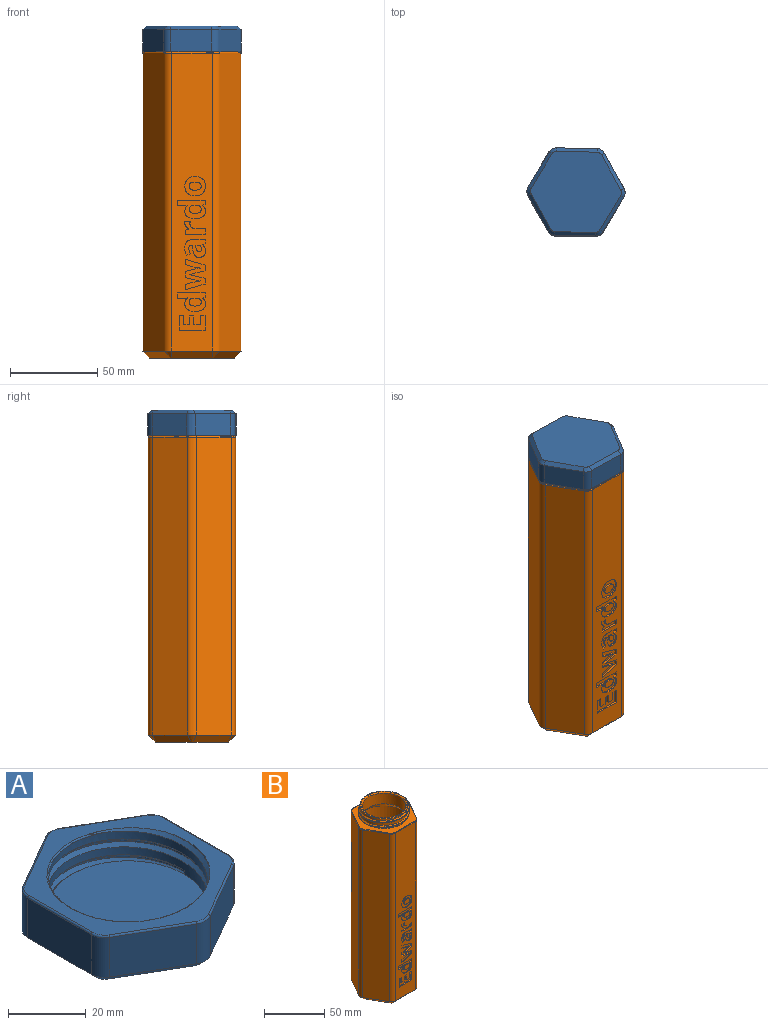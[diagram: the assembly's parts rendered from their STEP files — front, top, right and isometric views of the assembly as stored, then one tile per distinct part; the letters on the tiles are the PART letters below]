
ASSEMBLY  parts=2 mates=1
PART A: 48 faces, bbox 50.8x57x16.4 mm
  f0: cylinder r=20.5mm len=41mm, axis (0,0,1), area 638.7mm2, adj f9,f10,f12,f13,f15,f47
  f1: plane 20x12.5mm, normal (0.5,-0.87,0), area 288.7mm2, adj f16,f21,f26,f34
  f2: plane 23.09x12.5mm, normal (1,0,0), area 288.7mm2, adj f16,f17,f22,f37
  f3: plane 20x12.5mm, normal (0.5,0.87,0), area 288.7mm2, adj f17,f18,f25,f41
  f4: plane 20x12.5mm, normal (-0.5,0.87,0), area 288.7mm2, adj f18,f19,f29,f45
  f5: plane 23.09x12.5mm, normal (-1,0,0), area 288.7mm2, adj f19,f20,f33,f42
  f6: plane 20x12.5mm, normal (-0.5,-0.87,0), area 288.7mm2, adj f20,f21,f30,f38
  f7: plane 55.19x49mm, normal (0,0,1), area 683.1mm2, adj f10,f13,f14,f15,f22,f23,f24,f25
  f8: plane 52.19x46mm, normal (0,0,-1), area 1829.6mm2, adj f34,f35,f36,f37,f38,f39,f40,f41
  f9: plane 41x41mm, normal (0,0,1), area 1320.3mm2, adj f0,f11
  f10: torus R=20.9mm, axis (0,0,1), area 45.3mm2, adj f0,f7,f13,f15
  f11: cylinder r=20.5mm len=20.5mm, axis (0,0,-1), area 20.1mm2, adj f9,f12,f13
  f12: plane 2.36x0.9mm, normal (0,1,0), area 1.3mm2, adj f0,f11,f13,f46,f47
  f13: bspline ~49.65x43mm, area 400.1mm2, adj f0,f7,f10,f11,f12,f14,f46
  f14: cylinder r=21.5mm len=43mm, axis (0,0,-1), area 135.1mm2, adj f7,f13,f15,f46
  f15: bspline ~49.65x43mm, area 343.9mm2, adj f0,f7,f10,f14,f46,f47
  f16: cylinder r=5mm len=12.5mm, axis (0,0,-1), area 65.4mm2, adj f1,f2,f24,f35
  f17: cylinder r=5mm len=12.5mm, axis (0,0,-1), area 65.4mm2, adj f2,f3,f23,f39
  f18: cylinder r=5mm len=12.5mm, axis (0,0,-1), area 65.4mm2, adj f3,f4,f27,f43
  f19: cylinder r=5mm len=12.5mm, axis (0,0,-1), area 65.4mm2, adj f4,f5,f31,f44
  f20: cylinder r=5mm len=12.5mm, axis (0,0,-1), area 65.4mm2, adj f5,f6,f32,f40
  f21: cylinder r=5mm len=12.5mm, axis (0,0,-1), area 65.4mm2, adj f1,f6,f28,f36
  f22: cylinder r=0.5mm len=23.09mm, axis (0,-1,0), area 18.1mm2, adj f2,f7,f23,f24
  f23: torus R=4.5mm, axis (0,0,1), area 4mm2, adj f7,f17,f22,f25
  f24: torus R=4.5mm, axis (0,0,1), area 4mm2, adj f7,f16,f22,f26
  f25: cylinder r=0.5mm len=20.25mm, axis (0.87,-0.5,0), area 18.1mm2, adj f3,f7,f23,f27
  f26: cylinder r=0.5mm len=20.25mm, axis (-0.87,-0.5,0), area 18.1mm2, adj f1,f7,f24,f28
  f27: torus R=4.5mm, axis (0,0,1), area 4mm2, adj f7,f18,f25,f29
  f28: torus R=4.5mm, axis (0,0,1), area 4mm2, adj f7,f21,f26,f30
  f29: cylinder r=0.5mm len=20.25mm, axis (0.87,0.5,0), area 18.1mm2, adj f4,f7,f27,f31
  f30: cylinder r=0.5mm len=20.25mm, axis (-0.87,0.5,0), area 18.1mm2, adj f6,f7,f28,f32
  f31: torus R=4.5mm, axis (0,0,1), area 4mm2, adj f7,f19,f29,f33
  f32: torus R=4.5mm, axis (0,0,1), area 4mm2, adj f7,f20,f30,f33
  f33: cylinder r=0.5mm len=23.09mm, axis (0,1,0), area 18.1mm2, adj f5,f7,f31,f32
  f34: plane 21x13.28mm, normal (0.35,-0.61,-0.71), area 65.3mm2, adj f1,f8,f35,f36
  f35: cone r=3mm half-angle=45deg, axis (0,0,1), area 11.8mm2, adj f8,f16,f34,f37
  f36: cone r=3mm half-angle=45deg, axis (0,0,1), area 11.8mm2, adj f8,f21,f34,f38
  f37: plane 23.09x2mm, normal (0.71,0,-0.71), area 65.3mm2, adj f2,f8,f35,f39
  f38: plane 21x13.28mm, normal (-0.35,-0.61,-0.71), area 65.3mm2, adj f6,f8,f36,f40
  f39: cone r=3mm half-angle=45deg, axis (0,0,1), area 11.8mm2, adj f8,f17,f37,f41
  f40: cone r=3mm half-angle=45deg, axis (0,0,1), area 11.8mm2, adj f8,f20,f38,f42
  f41: plane 21x13.28mm, normal (0.35,0.61,-0.71), area 65.3mm2, adj f3,f8,f39,f43
  f42: plane 23.09x2mm, normal (-0.71,0,-0.71), area 65.3mm2, adj f5,f8,f40,f44
  f43: cone r=3mm half-angle=45deg, axis (0,0,1), area 11.8mm2, adj f8,f18,f41,f45
  f44: cone r=3mm half-angle=45deg, axis (0,0,1), area 11.8mm2, adj f8,f19,f42,f45
  f45: plane 21x13.28mm, normal (-0.35,0.61,-0.71), area 65.3mm2, adj f4,f8,f43,f44
  f46: cylinder r=0.1mm len=0.6mm, axis (0,0,-1), area 0.1mm2, adj f12,f13,f14,f15,f47
  f47: bspline ~1.47x1.47mm, area 0.2mm2, adj f0,f12,f15,f46
PART B: 211 faces, bbox 57.4x51.2x186.9 mm
  f0: plane 170.5x23.09mm, normal (0,-1,0), area 3247.6mm2, adj f17,f18,f36,f53,f60,f61,f62,f63
  f1: cylinder r=20mm len=40mm, axis (0,0,-1), area 682.5mm2, adj f2,f3,f9,f11,f14,f16
  f2: plane 2.3x1mm, normal (0,1,0), area 1.5mm2, adj f1,f3,f11,f12,f13,f16,f27,f28
  f3: bspline ~48.5x42mm, area 319.4mm2, adj f1,f2,f9,f16,f27
  f4: plane 170.5x20mm, normal (-0.87,-0.5,0), area 3937.5mm2, adj f17,f22,f40,f49
  f5: plane 170.5x20mm, normal (0.87,-0.5,0), area 3937.5mm2, adj f18,f19,f32,f57
  f6: plane 170.5x20mm, normal (0.87,0.5,0), area 3937.5mm2, adj f19,f20,f35,f54
  f7: plane 170.5x23.09mm, normal (0,1,0), area 3937.5mm2, adj f20,f21,f39,f50
  f8: plane 170.5x20mm, normal (-0.87,0.5,0), area 3937.5mm2, adj f21,f22,f43,f46
  f9: plane 55.57x49.38mm, normal (0,0,1), area 777.8mm2, adj f1,f3,f11,f12,f27,f28,f32,f33
  f10: plane 48.19x42mm, normal (0,0,-1), area 1492.5mm2, adj f44,f46,f47,f48,f49,f50,f51,f52
  f11: bspline ~48.5x42mm, area 268.8mm2, adj f1,f2,f9,f28
  f12: cylinder r=21mm len=42mm, axis (0,0,-1), area 66.2mm2, adj f2,f9,f27,f28
  f13: plane 0.93x0.06mm, normal (0,0,1), area 0mm2, adj f2,f14,f16
  f14: torus R=19.8mm, axis (0,0,1), area 39.3mm2, adj f1,f13,f15
  f15: plane 39.6x39.6mm, normal (0,0,1), area 97.5mm2, adj f14,f59
  f16: bspline ~10.06x3.04mm, area 1.4mm2, adj f1,f2,f3,f13
  f17: cylinder r=5mm len=170.5mm, axis (0,0,-1), area 892.7mm2, adj f0,f4,f38,f51
  f18: cylinder r=5mm len=170.5mm, axis (0,0,-1), area 892.7mm2, adj f0,f5,f34,f55
  f19: cylinder r=5mm len=170.5mm, axis (0,0,-1), area 892.7mm2, adj f5,f6,f33,f56
  f20: cylinder r=5mm len=170.5mm, axis (0,0,-1), area 892.7mm2, adj f6,f7,f37,f52
  f21: cylinder r=5mm len=170.5mm, axis (0,0,-1), area 892.7mm2, adj f7,f8,f41,f48
  f22: cylinder r=5mm len=170.5mm, axis (0,0,-1), area 892.7mm2, adj f4,f8,f42,f47
  f23: plane 36x36mm, normal (0,0,1), area 1004.7mm2, adj f31,f58
  f24: cylinder r=22mm len=159.46mm, axis (0,0,-1), area 22042.6mm2, adj f25,f58
  f25: cone r=22mm half-angle=40deg, axis (0,0,-1), area 782mm2, adj f24,f26
  f26: cylinder r=18mm len=36mm, axis (0,0,-1), area 1218mm2, adj f25,f59
  f27: bspline ~42.02x42.01mm, area 46.5mm2, adj f2,f3,f9,f12
  f28: bspline ~42.02x42.01mm, area 44.1mm2, adj f2,f9,f11,f12
  f29: cone r=1.5mm half-angle=26.3deg, axis (0,0.17,-0.98), area 19.6mm2, adj f44,f45
  f30: cylinder r=1.5mm len=3.15mm, axis (0,-0.17,0.98), area 10.7mm2, adj f31,f45
  f31: cone r=3.38mm half-angle=29.1deg, axis (0,0.17,-0.98), area 12mm2, adj f23,f30
  f32: cylinder r=0.5mm len=20.25mm, axis (-0.5,-0.87,0), area 18.1mm2, adj f5,f9,f33,f34
  f33: torus R=4.5mm, axis (0,0,1), area 4mm2, adj f9,f19,f32,f35
  f34: torus R=4.5mm, axis (0,0,1), area 4mm2, adj f9,f18,f32,f36
  f35: cylinder r=0.5mm len=20.25mm, axis (0.5,-0.87,0), area 18.1mm2, adj f6,f9,f33,f37
  f36: cylinder r=0.5mm len=23.09mm, axis (-1,0,0), area 18.1mm2, adj f0,f9,f34,f38
  f37: torus R=4.5mm, axis (0,0,1), area 4mm2, adj f9,f20,f35,f39
  f38: torus R=4.5mm, axis (0,0,1), area 4mm2, adj f9,f17,f36,f40
  f39: cylinder r=0.5mm len=23.09mm, axis (1,0,0), area 18.1mm2, adj f7,f9,f37,f41
  f40: cylinder r=0.5mm len=20.25mm, axis (-0.5,0.87,0), area 18.1mm2, adj f4,f9,f38,f42
  f41: torus R=4.5mm, axis (0,0,1), area 4mm2, adj f9,f21,f39,f43
  f42: torus R=4.5mm, axis (0,0,1), area 4mm2, adj f9,f22,f40,f43
  f43: cylinder r=0.5mm len=20.25mm, axis (0.5,0.87,0), area 18.1mm2, adj f8,f9,f41,f42
  f44: bspline ~6.73x6.6mm, area 10.7mm2, adj f10,f29
  f45: torus R=9.5mm, axis (0,0.17,-0.98), area 41mm2, adj f29,f30
  f46: plane 22x15.01mm, normal (-0.61,0.35,-0.71), area 130.6mm2, adj f8,f10,f47,f48
  f47: cone r=1mm half-angle=45deg, axis (0,0,1), area 17.8mm2, adj f10,f22,f46,f49
  f48: cone r=1mm half-angle=45deg, axis (0,0,1), area 17.8mm2, adj f10,f21,f46,f50
  f49: plane 22x15.01mm, normal (-0.61,-0.35,-0.71), area 130.6mm2, adj f4,f10,f47,f51
  f50: plane 23.09x4mm, normal (0,0.71,-0.71), area 130.6mm2, adj f7,f10,f48,f52
  f51: cone r=1mm half-angle=45deg, axis (0,0,1), area 17.8mm2, adj f10,f17,f49,f53
  f52: cone r=1mm half-angle=45deg, axis (0,0,1), area 17.8mm2, adj f10,f20,f50,f54
  f53: plane 23.09x4mm, normal (0,-0.71,-0.71), area 130.6mm2, adj f0,f10,f51,f55
  f54: plane 22x15.01mm, normal (0.61,0.35,-0.71), area 130.6mm2, adj f6,f10,f52,f56
  f55: cone r=1mm half-angle=45deg, axis (0,0,1), area 17.8mm2, adj f10,f18,f53,f57
  f56: cone r=1mm half-angle=45deg, axis (0,0,1), area 17.8mm2, adj f10,f19,f54,f57
  f57: plane 22x15.01mm, normal (0.61,-0.35,-0.71), area 130.6mm2, adj f5,f10,f55,f56
  f58: cone r=22mm half-angle=45deg, axis (0,0,1), area 710.9mm2, adj f23,f24
  f59: torus R=19mm, axis (0,0,1), area 181.2mm2, adj f15,f26
  f60: extruded ~4.34x1.47mm, area 4.7mm2, adj f0,f61,f77,f78
  f61: extruded ~3.12x1mm, area 3.2mm2, adj f0,f60,f62,f78
  f62: extruded ~2.04x1.92mm, area 2.8mm2, adj f0,f61,f63,f78
  f63: extruded ~2.89x1mm, area 3mm2, adj f0,f62,f64,f78
  f64: extruded ~4.09x1.55mm, area 4.5mm2, adj f0,f63,f65,f78
  f65: extruded ~4.33x1.45mm, area 4.7mm2, adj f0,f64,f66,f78
  f66: extruded ~3.13x1mm, area 3.2mm2, adj f0,f65,f67,f78
  f67: extruded ~2.06x1.92mm, area 2.9mm2, adj f0,f66,f68,f78
  f68: extruded ~2.89x1mm, area 3mm2, adj f0,f67,f77,f78
  f69: extruded ~2.55x1mm, area 2.6mm2, adj f70,f76,f78,f79
  f70: extruded ~2.54x1mm, area 2.6mm2, adj f69,f71,f78,f79
  f71: extruded ~1.79x1mm, area 2.1mm2, adj f70,f72,f78,f79
  f72: extruded ~1.8x1mm, area 2.1mm2, adj f71,f73,f78,f79
  f73: extruded ~2.53x1mm, area 2.6mm2, adj f72,f74,f78,f79
  f74: extruded ~2.56x1mm, area 2.6mm2, adj f73,f75,f78,f79
  f75: extruded ~1.79x1mm, area 2.1mm2, adj f74,f76,f78,f79
  f76: extruded ~1.81x1mm, area 2.1mm2, adj f69,f75,f78,f79
  f77: extruded ~4.08x1.57mm, area 4.5mm2, adj f0,f60,f68,f78
  f78: plane 11.79x11.03mm, normal (0,-1,0), area 79.2mm2, adj f60,f61,f62,f63,f64,f65,f66,f67
  f79: plane 6.8x4.69mm, normal (0,-1,0), area 26.8mm2, adj f69,f70,f71,f72,f73,f74,f75,f76
  f80: extruded ~1.74x1mm, area 1.9mm2, adj f81,f102,f103,f208
  f81: extruded ~1.66x1mm, area 1.9mm2, adj f80,f82,f103,f208
  f82: extruded ~2.52x1mm, area 2.6mm2, adj f81,f83,f103,f208
  f83: extruded ~2.56x1mm, area 2.7mm2, adj f82,f84,f103,f208
  f84: extruded ~1.61x1mm, area 1.9mm2, adj f83,f85,f103,f208
  f85: extruded ~1.84x1mm, area 2.1mm2, adj f84,f86,f103,f208
  f86: extruded ~2.63x1mm, area 2.7mm2, adj f85,f87,f103,f208
  f87: plane 1x0.34mm, normal (0,0,1), area 0.3mm2, adj f86,f102,f103,f208
  f88: extruded ~3.15x1.56mm, area 3.7mm2, adj f0,f89,f101,f103
  f89: extruded ~3.23x1.68mm, area 3.8mm2, adj f0,f88,f90,f103
  f90: plane 1x0.13mm, normal (-1,0,0), area 0.1mm2, adj f0,f89,f91,f103
  f91: plane 1.47x1mm, normal (-0.38,0,0.93), area 1.6mm2, adj f0,f90,f92,f103
  f92: plane 2.38x1mm, normal (-1,0,0), area 2.4mm2, adj f0,f91,f93,f103
  f93: plane 15.83x1mm, normal (0,0,-1), area 15.8mm2, adj f0,f92,f94,f103
  f94: plane 3.11x1mm, normal (1,0,0), area 3.1mm2, adj f0,f93,f95,f103
  f95: plane 3.64x1mm, normal (0,0,1), area 3.6mm2, adj f0,f94,f96,f103
  f96: extruded ~2.27x1mm, area 2.3mm2, adj f0,f95,f97,f103
  f97: plane 1x0.1mm, normal (1,0,0), area 0.1mm2, adj f0,f96,f98,f103
  f98: extruded ~3.28x1.67mm, area 3.8mm2, adj f0,f97,f99,f103
  f99: extruded ~3.21x1.56mm, area 3.7mm2, adj f0,f98,f100,f103
  f100: extruded ~4.36x1.16mm, area 4.6mm2, adj f0,f99,f101,f103
  f101: extruded ~4.31x1.14mm, area 4.5mm2, adj f0,f88,f100,f103
  f102: extruded ~2.35x1mm, area 2.5mm2, adj f80,f87,f103,f208
  f103: plane 16.04x10.63mm, normal (0,-1,0), area 98.8mm2, adj f80,f81,f82,f83,f84,f85,f86,f87
  f104: plane 3.98x1mm, normal (-0.21,0,0.98), area 4.1mm2, adj f0,f105,f129,f130
  f105: plane 3.38x1mm, normal (-1,0,0), area 3.4mm2, adj f0,f104,f106,f130
  f106: plane 11.37x3.28mm, normal (-0.28,0,-0.96), area 11.8mm2, adj f0,f105,f107,f130
  f107: plane 3.04x1mm, normal (1,0,0), area 3mm2, adj f0,f106,f108,f130
  f108: plane 5.04x1.36mm, normal (0.26,0,0.97), area 5.2mm2, adj f0,f107,f109,f130
  f109: extruded ~1.73x1mm, area 1.8mm2, adj f0,f108,f110,f130
  f110: extruded ~2.01x1mm, area 2mm2, adj f0,f109,f111,f130
  f111: plane 1x0.06mm, normal (1,0,0), area 0.1mm2, adj f0,f110,f112,f130
  f112: extruded ~1x0.76mm, area 0.8mm2, adj f0,f111,f113,f130
  f113: extruded ~1x0.97mm, area 1mm2, adj f0,f112,f114,f130
  f114: extruded ~1x0.93mm, area 0.9mm2, adj f0,f113,f115,f130
  f115: extruded ~1x0.66mm, area 0.7mm2, adj f0,f114,f116,f130
  f116: plane 5.45x1.33mm, normal (0.24,0,-0.97), area 5.6mm2, adj f0,f115,f117,f130
  f117: plane 3.42x1mm, normal (1,0,0), area 3.4mm2, adj f0,f116,f118,f130
  f118: plane 5.45x1.4mm, normal (0.25,0,0.97), area 5.6mm2, adj f0,f117,f119,f130
  f119: plane 1x0.87mm, normal (0.18,0,0.98), area 0.9mm2, adj f0,f118,f120,f130
  f120: extruded ~2.45x1mm, area 2.5mm2, adj f0,f119,f121,f130
  f121: plane 1x0.06mm, normal (1,0,0), area 0.1mm2, adj f0,f120,f122,f130
  f122: extruded ~3.73x1mm, area 3.8mm2, adj f0,f121,f123,f130
  f123: plane 5.04x1.31mm, normal (0.25,0,-0.97), area 5.2mm2, adj f0,f122,f124,f130
  f124: plane 3.09x1mm, normal (1,0,0), area 3.1mm2, adj f0,f123,f125,f130
  f125: plane 11.37x3.23mm, normal (-0.27,0,0.96), area 11.8mm2, adj f0,f124,f126,f130
  f126: plane 3.34x1mm, normal (-1,0,0), area 3.3mm2, adj f0,f125,f127,f130
  f127: plane 9x2.08mm, normal (-0.22,0,-0.97), area 9.2mm2, adj f0,f126,f128,f130
  f128: plane 1x0.07mm, normal (-1,0,0), area 0.1mm2, adj f0,f127,f129,f130
  f129: plane 5.03x1.18mm, normal (-0.23,0,0.97), area 5.2mm2, adj f0,f104,f128,f130
  f130: plane 17.43x11.37mm, normal (0,-1,0), area 110.5mm2, adj f104,f105,f106,f107,f108,f109,f110,f111
  f131: extruded ~1.05x1mm, area 1.1mm2, adj f0,f132,f143,f144
  f132: extruded ~1.96x1mm, area 2.1mm2, adj f0,f131,f133,f144
  f133: extruded ~1.54x1.43mm, area 2.1mm2, adj f0,f132,f134,f144
  f134: plane 1x0.15mm, normal (1,0,0), area 0.1mm2, adj f0,f133,f135,f144
  f135: plane 1.91x1mm, normal (0.23,0,-0.97), area 2mm2, adj f0,f134,f136,f144
  f136: plane 2.35x1mm, normal (1,0,0), area 2.4mm2, adj f0,f135,f137,f144
  f137: plane 11.37x1mm, normal (0,0,1), area 11.4mm2, adj f0,f136,f138,f144
  f138: plane 3.1x1mm, normal (-1,0,0), area 3.1mm2, adj f0,f137,f139,f144
  f139: plane 5.79x1mm, normal (0,0,-1), area 5.8mm2, adj f0,f138,f140,f144
  f140: extruded ~2.14x1mm, area 2.4mm2, adj f0,f139,f141,f144
  f141: extruded ~2.31x1mm, area 2.5mm2, adj f0,f140,f142,f144
  f142: extruded ~1x0.91mm, area 0.9mm2, adj f0,f141,f143,f144
  f143: plane 2.91x1mm, normal (-0.08,0,-1), area 2.9mm2, adj f0,f131,f142,f144
  f144: plane 11.59x7.4mm, normal (0,-1,0), area 46.2mm2, adj f131,f132,f133,f134,f135,f136,f137,f138
  f145: extruded ~1.74x1mm, area 1.9mm2, adj f146,f167,f168,f209
  f146: extruded ~1.66x1mm, area 1.9mm2, adj f145,f147,f168,f209
  f147: extruded ~2.52x1mm, area 2.6mm2, adj f146,f148,f168,f209
  f148: extruded ~2.56x1mm, area 2.7mm2, adj f147,f149,f168,f209
  f149: extruded ~1.61x1mm, area 1.9mm2, adj f148,f150,f168,f209
  f150: extruded ~1.84x1mm, area 2.1mm2, adj f149,f151,f168,f209
  f151: extruded ~2.63x1mm, area 2.7mm2, adj f150,f152,f168,f209
  f152: plane 1x0.34mm, normal (0,0,1), area 0.3mm2, adj f151,f167,f168,f209
  f153: extruded ~3.15x1.56mm, area 3.7mm2, adj f0,f154,f166,f168
  f154: extruded ~3.23x1.68mm, area 3.8mm2, adj f0,f153,f155,f168
  f155: plane 1x0.13mm, normal (-1,0,0), area 0.1mm2, adj f0,f154,f156,f168
  f156: plane 1.47x1mm, normal (-0.38,0,0.93), area 1.6mm2, adj f0,f155,f157,f168
  f157: plane 2.38x1mm, normal (-1,0,0), area 2.4mm2, adj f0,f156,f158,f168
  f158: plane 15.83x1mm, normal (0,0,-1), area 15.8mm2, adj f0,f157,f159,f168
  f159: plane 3.11x1mm, normal (1,0,0), area 3.1mm2, adj f0,f158,f160,f168
  f160: plane 3.64x1mm, normal (0,0,1), area 3.6mm2, adj f0,f159,f161,f168
  f161: extruded ~2.27x1mm, area 2.3mm2, adj f0,f160,f162,f168
  f162: plane 1x0.1mm, normal (1,0,0), area 0.1mm2, adj f0,f161,f163,f168
  f163: extruded ~3.28x1.67mm, area 3.8mm2, adj f0,f162,f164,f168
  f164: extruded ~3.21x1.56mm, area 3.7mm2, adj f0,f163,f165,f168
  f165: extruded ~4.36x1.16mm, area 4.6mm2, adj f0,f164,f166,f168
  f166: extruded ~4.31x1.14mm, area 4.5mm2, adj f0,f153,f165,f168
  f167: extruded ~2.35x1mm, area 2.5mm2, adj f145,f152,f168,f209
  f168: plane 16.04x10.63mm, normal (0,-1,0), area 98.8mm2, adj f145,f146,f147,f148,f149,f150,f151,f152
  f169: plane 1.2x1mm, normal (-1,0,-0.04), area 1.2mm2, adj f170,f193,f194,f210
  f170: plane 1x0.94mm, normal (0,0,1), area 0.9mm2, adj f169,f171,f194,f210
  f171: extruded ~1.65x1mm, area 1.8mm2, adj f170,f172,f194,f210
  f172: extruded ~1.73x1mm, area 1.9mm2, adj f171,f173,f194,f210
  f173: extruded ~1.5x1.32mm, area 2.3mm2, adj f172,f174,f194,f210
  f174: extruded ~1.36x1mm, area 1.6mm2, adj f173,f193,f194,f210
  f175: plane 1.55x1mm, normal (-0.36,0,0.93), area 1.7mm2, adj f0,f176,f192,f194
  f176: plane 2.16x1mm, normal (-1,0,0), area 2.2mm2, adj f0,f175,f177,f194
  f177: plane 7.58x1mm, normal (0,0,-1), area 7.6mm2, adj f0,f176,f178,f194
  f178: extruded ~3.03x1.22mm, area 3.4mm2, adj f0,f177,f179,f194
  f179: extruded ~3.51x1mm, area 3.7mm2, adj f0,f178,f180,f194
  f180: extruded ~4.35x1.03mm, area 4.5mm2, adj f0,f179,f181,f194
  f181: plane 2.1x1.03mm, normal (-0.44,0,0.9), area 2.3mm2, adj f0,f180,f182,f194
  f182: extruded ~3.21x1mm, area 3.3mm2, adj f0,f181,f183,f194
  f183: extruded ~1.77x1.73mm, area 2.8mm2, adj f0,f182,f184,f194
  f184: plane 1x0.5mm, normal (0,0,1), area 0.5mm2, adj f0,f183,f185,f194
  f185: plane 1.98x1mm, normal (1,0,0.03), area 2mm2, adj f0,f184,f186,f194
  f186: extruded ~3.82x1mm, area 4mm2, adj f0,f185,f187,f194
  f187: extruded ~2.67x1.27mm, area 3.1mm2, adj f0,f186,f188,f194
  f188: extruded ~2.67x1mm, area 2.9mm2, adj f0,f187,f189,f194
  f189: extruded ~2.58x1mm, area 2.8mm2, adj f0,f188,f190,f194
  f190: extruded ~2.16x1mm, area 2.2mm2, adj f0,f189,f191,f194
  f191: extruded ~1.61x1.37mm, area 2.1mm2, adj f0,f190,f192,f194
  f192: plane 1x0.08mm, normal (-1,0,0), area 0.1mm2, adj f0,f175,f191,f194
  f193: extruded ~2.02x1mm, area 2.1mm2, adj f169,f174,f194,f210
  f194: plane 11.81x10.14mm, normal (0,-1,0), area 79.3mm2, adj f169,f170,f171,f172,f173,f174,f175,f176
  f195: plane 8.56x1mm, normal (-1,0,0), area 8.6mm2, adj f0,f196,f206,f207
  f196: plane 2.6x1mm, normal (0,0,-1), area 2.6mm2, adj f0,f195,f197,f207
  f197: plane 5.41x1mm, normal (1,0,0), area 5.4mm2, adj f0,f196,f198,f207
  f198: plane 3.83x1mm, normal (0,0,-1), area 3.8mm2, adj f0,f197,f199,f207
  f199: plane 5.04x1mm, normal (-1,0,0), area 5mm2, adj f0,f198,f200,f207
  f200: plane 2.58x1mm, normal (0,0,-1), area 2.6mm2, adj f0,f199,f201,f207
  f201: plane 5.04x1mm, normal (1,0,0), area 5mm2, adj f0,f200,f202,f207
  f202: plane 3.27x1mm, normal (0,0,-1), area 3.3mm2, adj f0,f201,f203,f207
  f203: plane 5.41x1mm, normal (-1,0,0), area 5.4mm2, adj f0,f202,f204,f207
  f204: plane 2.58x1mm, normal (0,0,-1), area 2.6mm2, adj f0,f203,f205,f207
  f205: plane 8.56x1mm, normal (1,0,0), area 8.6mm2, adj f0,f204,f206,f207
  f206: plane 14.87x1mm, normal (0,0,1), area 14.9mm2, adj f0,f195,f205,f207
  f207: plane 14.87x8.56mm, normal (0,-1,0), area 88mm2, adj f195,f196,f197,f198,f199,f200,f201,f202
  f208: plane 6.79x4.59mm, normal (0,-1,0), area 26.2mm2, adj f80,f81,f82,f83,f84,f85,f86,f87
  f209: plane 6.79x4.59mm, normal (0,-1,0), area 26.2mm2, adj f145,f146,f147,f148,f149,f150,f151,f152
  f210: plane 3.88x3.21mm, normal (0,-1,0), area 10.1mm2, adj f169,f170,f171,f172,f173,f174,f193
PLACE A rot(axis=(0.71,0.7,0),180deg) t=(-91.85,-93.61,175.29)mm
PLACE B t=(-91.85,-93.61,-14.71)mm fixed
MATE revolute B.f1 <-> A.f0  axis (0,0,1) through (-91.85,-93.61,170.29)mm
